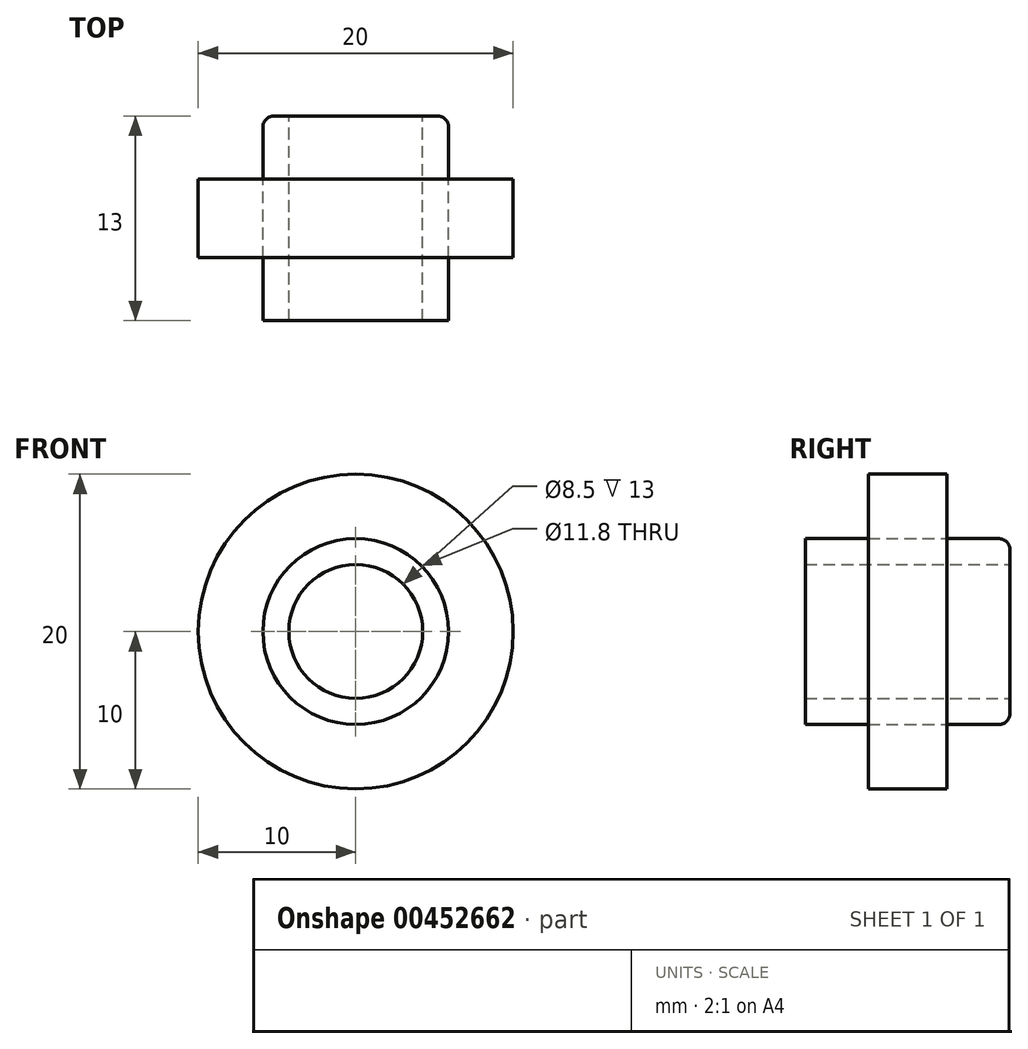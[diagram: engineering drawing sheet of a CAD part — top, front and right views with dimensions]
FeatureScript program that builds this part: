
annotation { "Feature Type Name" : "Feature", "Feature Type Description" : "" }
export const myFeature = defineFeature(function(context is Context, id is Id, definition is map)
    precondition{}
    {
        {
            var Q0;
            Q0=qCreatedBy(makeId("Front.planeOp"),FACE);
            var sketch = newSketch(context, id + "F0", { "sketchPlane" : qUnion([Q0])});
            skCircle(sketch, "E0", {"center": v(0, 0) * mm, "radius": 5.9 * mm});
            skCircle(sketch, "E1", {"center": v(0, 0) * mm, "radius": 10 * mm});
            skCircle(sketch, "E2", {"center": v(0, 0) * mm, "radius": 4.25 * mm});
            skSolve(sketch);
        }
        {
            var Q0;
            Q0=makeQuery(id+"F0.imprint","IMPRINT",FACE,{"disambiguationData":[TD([[makeQuery(id+"F0.imprint","IMPRINT",EDGE,{"derivedFrom":sQuery(id+"F0.wireOp",EDGE,"E0")}),-1.0]])]});
            extrude(context, id + "F1", {"entities" : qUnion([Q0]), "endBound" : BoundingType.SYMMETRIC, "depth" : 5 * mm});
        }
        {
            var Q0;
            Q0=makeQuery(id+"F0.imprint","IMPRINT",FACE,{"disambiguationData":[TD([[makeQuery(id+"F0.imprint","IMPRINT",EDGE,{"derivedFrom":sQuery(id+"F0.wireOp",EDGE,"E0")}),1.0]])]});
            extrude(context, id + "F2", {"entities" : qUnion([Q0]), "endBound" : BoundingType.SYMMETRIC, "depth" : 13 * mm});
        }
        {
            var Q0;
            Q0=makeQuery(id+"F2.opExtrude","CAP_EDGE",EDGE,{"disambiguationData":[OSD([sQuery(id+"F0.wireOp",EDGE,"E0")])],"isStart":true});
            fillet(context, id + "F3", {"entities" : qUnion([Q0]), "radius" : 0.7 * mm, "tangentPropagation" : true, "allowEdgeOverflow" : false});
        }
    });
